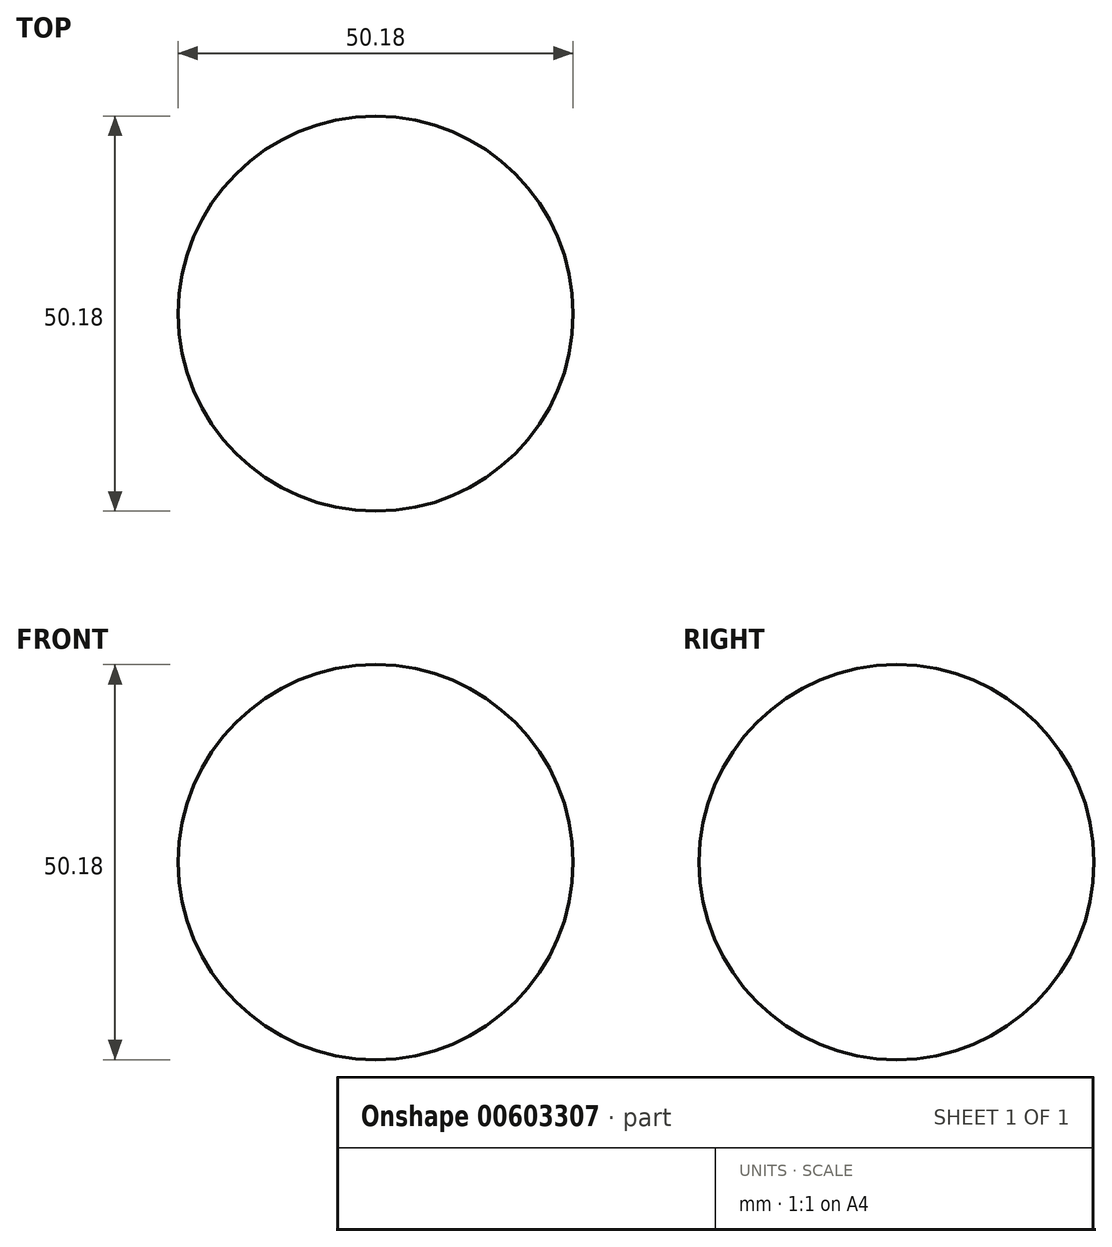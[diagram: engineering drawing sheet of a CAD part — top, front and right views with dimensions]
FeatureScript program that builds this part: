
annotation { "Feature Type Name" : "Feature", "Feature Type Description" : "" }
export const myFeature = defineFeature(function(context is Context, id is Id, definition is map)
    precondition{}
    {
        {
            var Q0;
            Q0=qCreatedBy(makeId("Top.planeOp"),FACE);
            var sketch = newSketch(context, id + "F0", { "sketchPlane" : qUnion([Q0])});
            skCircle(sketch, "E0", {"center": v(0, 0) * mm, "radius": 25.1 * mm});
            skLineSegment(sketch, "E1", {"start": v(-36.68, 0) * mm, "end": v(54.52, 0) * mm});
            skSolve(sketch);
        }
        {
            var Q0;
            {var subQ0=sQuery(id+"F0.wireOp",EDGE,"E1");var subQ1=sQuery(id+"F0.wireOp",EDGE,"E0");var subQ2=makeQuery(id+"F0.imprint","INTERSECT",VERTEX,{"disambiguationData":[OD(0.0)],"derivedFrom":[subQ1,subQ0]});Q0=makeQuery(id+"F0.imprint","IMPRINT",FACE,{"disambiguationData":[TD([[makeQuery(id+"F0.imprint","IMPRINT",EDGE,{"disambiguationData":[TD([[subQ2,-1.0]])],"derivedFrom":subQ1}),1.0]])]});}
            var Q1;
            Q1=sQuery(id+"F0.wireOp",EDGE,"E1");
            revolve(context, id + "F1", {"entities" : qUnion([Q0]), "axis" : qUnion([Q1]), "revolveType" : RevolveType.FULL});
        }
    });
